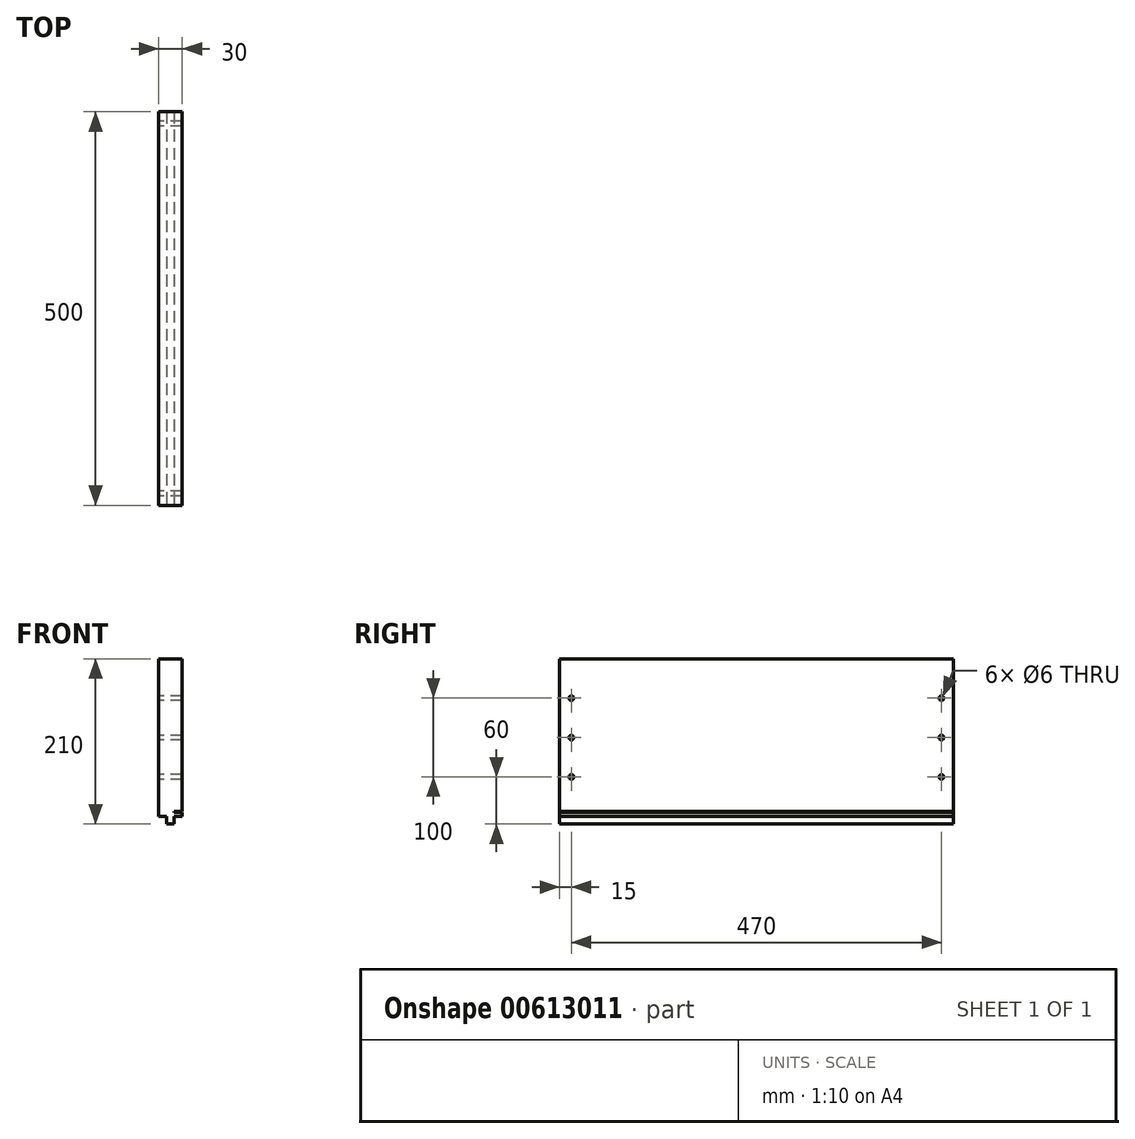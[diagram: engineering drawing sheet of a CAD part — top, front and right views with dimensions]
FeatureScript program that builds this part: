
annotation { "Feature Type Name" : "Feature", "Feature Type Description" : "" }
export const myFeature = defineFeature(function(context is Context, id is Id, definition is map)
    precondition{}
    {
        {
            var Q0;
            Q0=qCreatedBy(makeId("Right.planeOp"),FACE);
            var sketch = newSketch(context, id + "F0", { "sketchPlane" : qUnion([Q0])});
            skLineSegment(sketch, "E0.bottom", {"start": v(250, -100) * mm, "end": v(-250, -100) * mm});
            skLineSegment(sketch, "E0.top", {"start": v(250, 100) * mm, "end": v(-250, 100) * mm});
            skLineSegment(sketch, "E0.left", {"start": v(250, -100) * mm, "end": v(250, 100) * mm});
            skLineSegment(sketch, "E0.right", {"start": v(-250, -100) * mm, "end": v(-250, 100) * mm});
            skPoint(sketch, "E0.middle", {"position": v(0, 0) * mm});
            skCircle(sketch, "E1", {"center": v(-235, 50) * mm, "radius": 3 * mm});
            skCircle(sketch, "E2", {"center": v(235, -50) * mm, "radius": 3 * mm});
            skCircle(sketch, "E3", {"center": v(235, 50) * mm, "radius": 3 * mm});
            skCircle(sketch, "E4", {"center": v(-235, -50) * mm, "radius": 3 * mm});
            skCircle(sketch, "E5", {"center": v(-235, 0) * mm, "radius": 3 * mm});
            skCircle(sketch, "E6", {"center": v(235, 0) * mm, "radius": 3 * mm});
            skSolve(sketch);
        }
        {
            var Q0;
            Q0=qSketchRegion(id+"F0",true);
            extrude(context, id + "F1", {"entities" : qUnion([Q0]), "depth" : 30 * mm, "offsetDistance" : 25 * mm});
        }
        {
            var Q0;
            Q0=makeQuery(id+"F1.opExtrude","SWEPT_FACE",FACE,{"disambiguationData":[OSD([sQuery(id+"F0.wireOp",EDGE,"E0.right")])]});
            var sketch = newSketch(context, id + "F2", { "sketchPlane" : qUnion([Q0])});
            skLineSegment(sketch, "E7.bottom", {"start": v(20, -110) * mm, "end": v(10, -110) * mm});
            skLineSegment(sketch, "E7.top", {"start": v(20, -100) * mm, "end": v(10, -100) * mm});
            skLineSegment(sketch, "E7.left", {"start": v(20, -110) * mm, "end": v(20, -100) * mm});
            skLineSegment(sketch, "E7.right", {"start": v(10, -110) * mm, "end": v(10, -100) * mm});
            skPoint(sketch, "E7.middle", {"position": v(15, -105) * mm});
            skSolve(sketch);
        }
        {
            var Q0;
            Q0 = qSketchRegion(id + "F2", true);
            extrude(context, id + "F3", {"entities" : qUnion([Q0]), "operationType" : NewBodyOperationType.ADD, "oppositeDirection" : true, "depth" : 500 * mm, "offsetDistance" : 25 * mm});
        }
        {
            var Q0;
            Q0=makeQuery(id+"F3.boolean.opBoolean","MERGE",FACE,{"derivedFrom":[makeQuery(id+"F1.opExtrude","SWEPT_FACE",FACE,{"disambiguationData":[OSD([sQuery(id+"F0.wireOp",EDGE,"E0.right")])]}),makeQuery(id+"F3.opExtrude","CAP_FACE",FACE,{"disambiguationData":[OSD([sQuery(id+"F2.wireOp",EDGE,"E7.bottom"),sQuery(id+"F2.wireOp",EDGE,"E7.top"),sQuery(id+"F2.wireOp",EDGE,"E7.left"),sQuery(id+"F2.wireOp",EDGE,"E7.right")])],"isStart":true})]});
            var sketch = newSketch(context, id + "F4", { "sketchPlane" : qUnion([Q0])});
            skLineSegment(sketch, "E8.bottom", {"start": v(30, -95) * mm, "end": v(20, -95) * mm});
            skLineSegment(sketch, "E8.top", {"start": v(30, -94) * mm, "end": v(20, -94) * mm});
            skLineSegment(sketch, "E8.left", {"start": v(30, -95) * mm, "end": v(30, -94) * mm});
            skLineSegment(sketch, "E8.right", {"start": v(20, -95) * mm, "end": v(20, -94) * mm});
            skPoint(sketch, "E8.middle", {"position": v(25, -94.5) * mm});
            skSolve(sketch);
        }
        {
            var Q0;
            Q0 = qSketchRegion(id + "F4", true);
            extrude(context, id + "F5", {"entities" : qUnion([Q0]), "operationType" : NewBodyOperationType.REMOVE, "oppositeDirection" : true, "depth" : 500 * mm, "offsetDistance" : 25 * mm});
        }
    });
